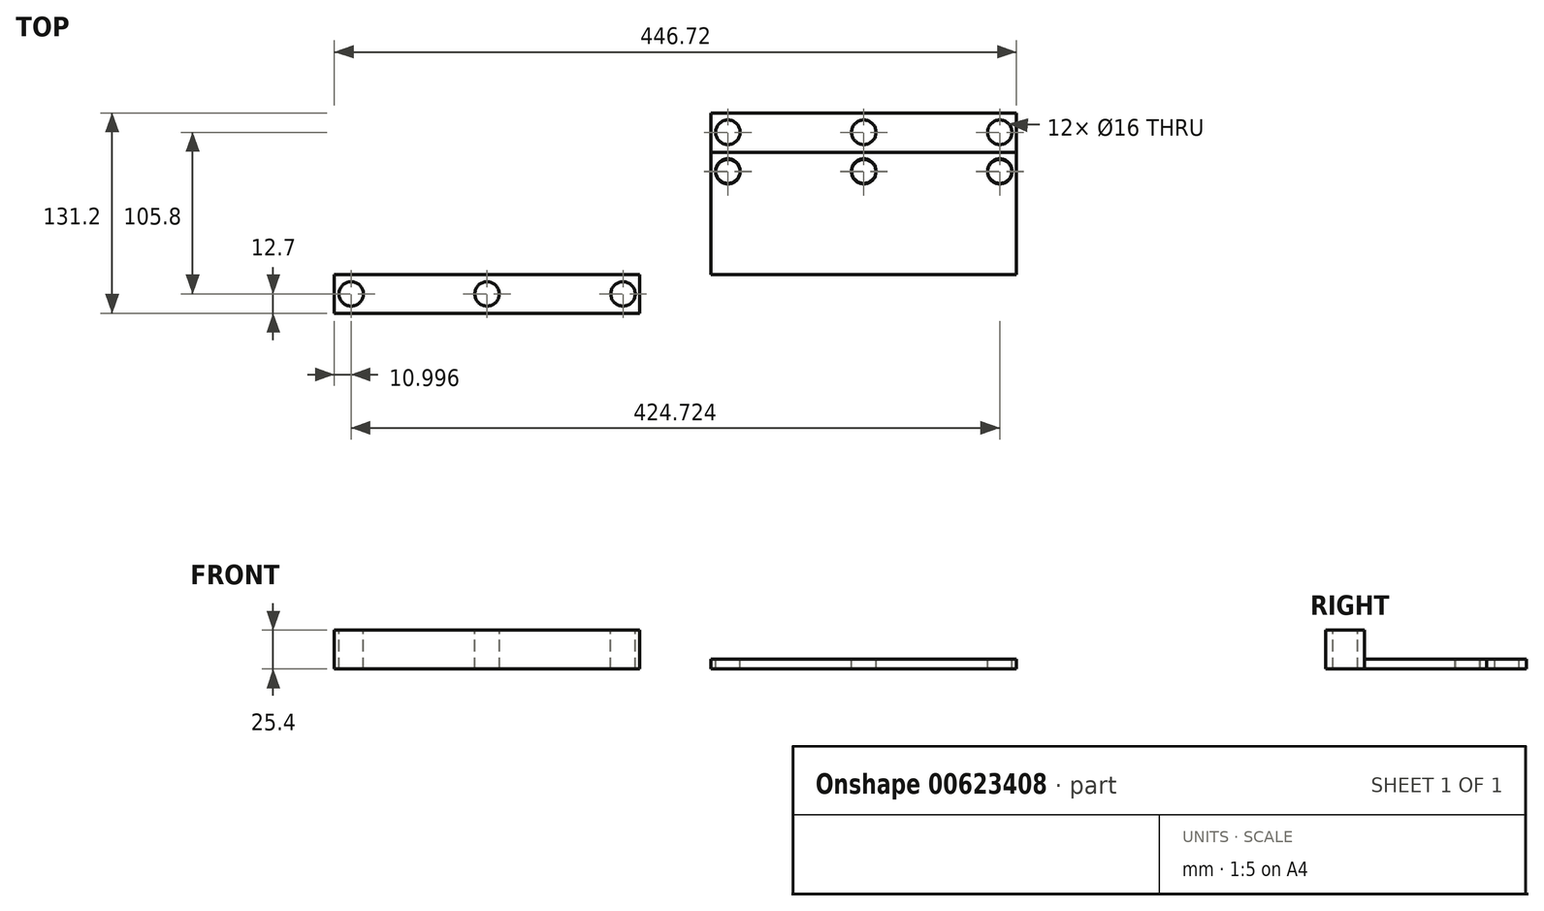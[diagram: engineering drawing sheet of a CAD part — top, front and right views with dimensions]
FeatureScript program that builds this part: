
annotation { "Feature Type Name" : "Feature", "Feature Type Description" : "" }
export const myFeature = defineFeature(function(context is Context, id is Id, definition is map)
    precondition{}
    {
        {
            var Q0;
            Q0=qCreatedBy(makeId("Top.planeOp"),FACE);
            var sketch = newSketch(context, id + "F0", { "sketchPlane" : qUnion([Q0])});
            skLineSegment(sketch, "E0.bottom", {"start": v(0, 0) * mm, "end": v(200, 0) * mm});
            skLineSegment(sketch, "E0.top", {"start": v(0, 80) * mm, "end": v(200, 80) * mm});
            skLineSegment(sketch, "E0.left", {"start": v(0, 0) * mm, "end": v(0, 80) * mm});
            skLineSegment(sketch, "E0.right", {"start": v(200, 0) * mm, "end": v(200, 80) * mm});
            skSolve(sketch);
        }
        {
            var Q0;
            Q0 = qSketchRegion(id + "F0", true);
            extrude(context, id + "F1", {"entities" : qUnion([Q0]), "depth" : 6.35 * mm, "offsetDistance" : 25.4 * mm});
        }
        {
            var Q0;
            Q0=makeQuery(id+"F1.opExtrude","CAP_FACE",FACE,{"disambiguationData":[OSD([sQuery(id+"F0.wireOp",EDGE,"E0.bottom"),sQuery(id+"F0.wireOp",EDGE,"E0.top"),sQuery(id+"F0.wireOp",EDGE,"E0.left"),sQuery(id+"F0.wireOp",EDGE,"E0.right")])],"isStart":false});
            var sketch = newSketch(context, id + "F2", { "sketchPlane" : qUnion([Q0])});
            skCircle(sketch, "E1", {"center": v(11, 67.3) * mm, "radius": 8 * mm});
            skCircle(sketch, "E2", {"center": v(100, 67.3) * mm, "radius": 8 * mm});
            skCircle(sketch, "E3", {"center": v(189, 67.3) * mm, "radius": 8 * mm});
            skLineSegment(sketch, "E4", {"start": v(0, 54.6) * mm, "end": v(200, 54.6) * mm});
            skSolve(sketch);
        }
        {
            var Q0;
            Q0=sQuery(id+"F2.wireOp",VERTEX,"E1.center");
            var Q1;
            Q1=sQuery(id+"F2.wireOp",VERTEX,"E2.center");
            var Q2;
            Q2=sQuery(id+"F2.wireOp",VERTEX,"E3.center");
            var Q3;
            Q3=makeQuery(id+"F1.opExtrude","SWEPT_BODY",BODY,{"disambiguationData":[OSD([sQuery(id+"F0.wireOp",EDGE,"E0.bottom"),sQuery(id+"F0.wireOp",EDGE,"E0.top"),sQuery(id+"F0.wireOp",EDGE,"E0.left"),sQuery(id+"F0.wireOp",EDGE,"E0.right")])]});
            hole(context, id + "F3", {"style" : HoleStyle.SIMPLE, "endStyle" : HoleEndStyle.THROUGH, "holeDiameter" : 16 * mm, "majorDiameter" : 6.35 * mm, "isTappedThrough" : true, "tappedDepth" : 12.7 * mm, "tapClearance" : 3, "locations" : qUnion([Q0, Q1, Q2]), "scope" : qUnion([Q3])});
        }
        {
            var Q0;
            Q0=qCreatedBy(makeId("Top.planeOp"),FACE);
            var sketch = newSketch(context, id + "F4", { "sketchPlane" : qUnion([Q0])});
            skLineSegment(sketch, "E5.bottom", {"start": v(-246.72, -25.4) * mm, "end": v(-46.72, -25.4) * mm});
            skLineSegment(sketch, "E5.top", {"start": v(-246.72, 0) * mm, "end": v(-46.72, 0) * mm});
            skLineSegment(sketch, "E5.left", {"start": v(-246.72, -25.4) * mm, "end": v(-246.72, 0) * mm});
            skLineSegment(sketch, "E5.right", {"start": v(-46.72, -25.4) * mm, "end": v(-46.72, 0) * mm});
            skSolve(sketch);
        }
        {
            var Q0;
            Q0=makeQuery(id+"F4.imprint","IMPRINT",FACE,{"disambiguationData":[TD([[makeQuery(id+"F4.imprint","IMPRINT",EDGE,{"derivedFrom":sQuery(id+"F4.wireOp",EDGE,"E5.bottom")}),1.0]])]});
            extrude(context, id + "F5", {"entities" : qUnion([Q0]), "depth" : 25.4 * mm, "offsetDistance" : 25.4 * mm});
        }
        {
            var Q0;
            Q0=makeQuery(id+"F5.opExtrude","CAP_FACE",FACE,{"disambiguationData":[OSD([sQuery(id+"F4.wireOp",EDGE,"E5.bottom"),sQuery(id+"F4.wireOp",EDGE,"E5.top"),sQuery(id+"F4.wireOp",EDGE,"E5.left"),sQuery(id+"F4.wireOp",EDGE,"E5.right")])],"isStart":false});
            var sketch = newSketch(context, id + "F6", { "sketchPlane" : qUnion([Q0])});
            skCircle(sketch, "E6", {"center": v(-235.72, -12.7) * mm, "radius": 8 * mm});
            skPoint(sketch, "E6.centerSnap0", {"position": v(-246.72, -12.7) * mm});
            skCircle(sketch, "E7", {"center": v(-57.72, -12.7) * mm, "radius": 8 * mm});
            skPoint(sketch, "E7.centerSnap0", {"position": v(-46.72, -12.7) * mm});
            skCircle(sketch, "E8", {"center": v(-146.72, -12.7) * mm, "radius": 8 * mm});
            skSolve(sketch);
        }
        {
            var Q0;
            Q0=sQuery(id+"F6.wireOp",VERTEX,"E7.center");
            var Q1;
            Q1=sQuery(id+"F6.wireOp",VERTEX,"E8.center");
            var Q2;
            Q2=sQuery(id+"F6.wireOp",VERTEX,"E6.center");
            var Q3;
            Q3=makeQuery(id+"F5.opExtrude","SWEPT_BODY",BODY,{"disambiguationData":[OSD([sQuery(id+"F4.wireOp",EDGE,"E5.bottom"),sQuery(id+"F4.wireOp",EDGE,"E5.top"),sQuery(id+"F4.wireOp",EDGE,"E5.left"),sQuery(id+"F4.wireOp",EDGE,"E5.right")])]});
            hole(context, id + "F7", {"style" : HoleStyle.SIMPLE, "endStyle" : HoleEndStyle.THROUGH, "holeDiameter" : 16 * mm, "majorDiameter" : 6.35 * mm, "isTappedThrough" : true, "tappedDepth" : 12.7 * mm, "tapClearance" : 3, "locations" : qUnion([Q0, Q1, Q2]), "scope" : qUnion([Q3])});
        }
        {
            var Q0;
            Q0=qCreatedBy(makeId("Top.planeOp"),FACE);
            var sketch = newSketch(context, id + "F8", { "sketchPlane" : qUnion([Q0])});
            skLineSegment(sketch, "E9.bottom", {"start": v(0, 0) * mm, "end": v(200, 0) * mm});
            skLineSegment(sketch, "E9.top", {"start": v(0, 105.8) * mm, "end": v(200, 105.8) * mm});
            skLineSegment(sketch, "E9.left", {"start": v(0, 0) * mm, "end": v(0, 105.8) * mm});
            skLineSegment(sketch, "E9.right", {"start": v(200, 0) * mm, "end": v(200, 105.8) * mm});
            skSolve(sketch);
        }
        {
            var Q0;
            Q0=makeQuery(id+"F8.imprint","IMPRINT",FACE,{"disambiguationData":[TD([[makeQuery(id+"F8.imprint","IMPRINT",EDGE,{"derivedFrom":sQuery(id+"F8.wireOp",EDGE,"E9.bottom")}),1.0]])]});
            extrude(context, id + "F9", {"entities" : qUnion([Q0]), "depth" : 6.35 * mm, "offsetDistance" : 25.4 * mm});
        }
        {
            var Q0;
            Q0=makeQuery(id+"F9.opExtrude","CAP_FACE",FACE,{"disambiguationData":[OSD([sQuery(id+"F8.wireOp",EDGE,"E9.bottom"),sQuery(id+"F8.wireOp",EDGE,"E9.top"),sQuery(id+"F8.wireOp",EDGE,"E9.left"),sQuery(id+"F8.wireOp",EDGE,"E9.right")])],"isStart":false});
            var sketch = newSketch(context, id + "F10", { "sketchPlane" : qUnion([Q0])});
            skCircle(sketch, "E10", {"center": v(189, 93.1) * mm, "radius": 8 * mm});
            skCircle(sketch, "E11", {"center": v(100, 93.1) * mm, "radius": 8 * mm});
            skPoint(sketch, "E11.centerSnap0", {"position": v(100, 105.8) * mm});
            skCircle(sketch, "E12", {"center": v(11, 93.1) * mm, "radius": 8 * mm});
            skCircle(sketch, "E13", {"center": v(11, 67.7) * mm, "radius": 8 * mm});
            skCircle(sketch, "E14", {"center": v(100, 67.7) * mm, "radius": 8 * mm});
            skCircle(sketch, "E15", {"center": v(189, 67.7) * mm, "radius": 8 * mm});
            skSolve(sketch);
        }
        {
            var Q0;
            Q0=sQuery(id+"F10.wireOp",VERTEX,"E12.center");
            var Q1;
            Q1=sQuery(id+"F10.wireOp",VERTEX,"E11.center");
            var Q2;
            Q2=sQuery(id+"F10.wireOp",VERTEX,"E10.center");
            var Q3;
            Q3=sQuery(id+"F10.wireOp",VERTEX,"E15.center");
            var Q4;
            Q4=sQuery(id+"F10.wireOp",VERTEX,"E14.center");
            var Q5;
            Q5=sQuery(id+"F10.wireOp",VERTEX,"E13.center");
            var Q6;
            Q6=makeQuery(id+"F9.opExtrude","SWEPT_BODY",BODY,{"disambiguationData":[OSD([sQuery(id+"F8.wireOp",EDGE,"E9.bottom"),sQuery(id+"F8.wireOp",EDGE,"E9.top"),sQuery(id+"F8.wireOp",EDGE,"E9.left"),sQuery(id+"F8.wireOp",EDGE,"E9.right")])]});
            hole(context, id + "F11", {"style" : HoleStyle.SIMPLE, "endStyle" : HoleEndStyle.THROUGH, "holeDiameter" : 16 * mm, "majorDiameter" : 6.35 * mm, "isTappedThrough" : true, "tappedDepth" : 12.7 * mm, "tapClearance" : 3, "locations" : qUnion([Q0, Q1, Q2, Q3, Q4, Q5]), "scope" : qUnion([Q6])});
        }
    });
